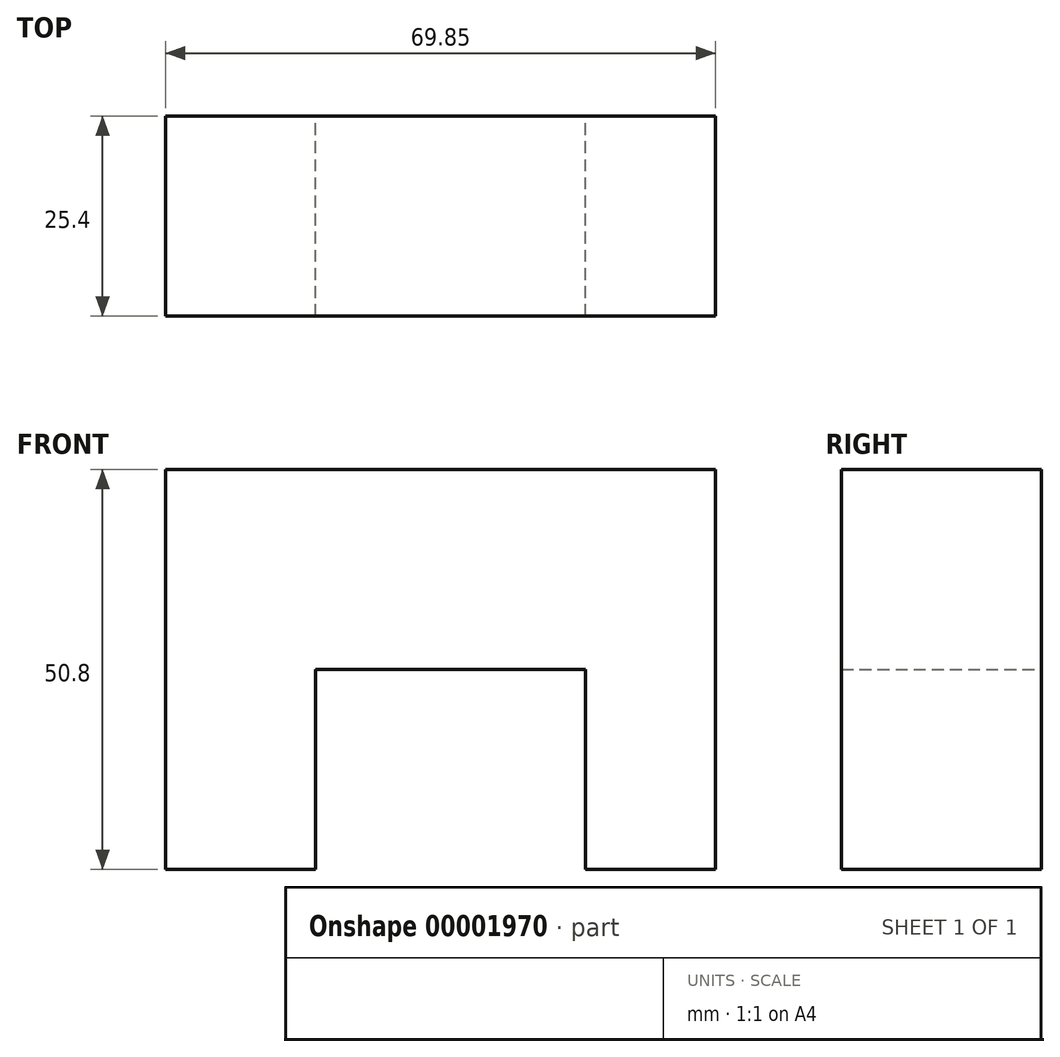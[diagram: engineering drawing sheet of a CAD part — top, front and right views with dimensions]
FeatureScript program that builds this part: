
annotation { "Feature Type Name" : "Feature", "Feature Type Description" : "" }
export const myFeature = defineFeature(function(context is Context, id is Id, definition is map)
    precondition{}
    {
        {
            var Q0;
            Q0=qCreatedBy(makeId("Front.planeOp"),FACE);
            var sketch = newSketch(context, id + "F0", { "sketchPlane" : qUnion([Q0])});
            skLineSegment(sketch, "E0.bottom", {"start": v(0, 0) * mm, "end": v(19.05, 0) * mm});
            skLineSegment(sketch, "E0.top", {"start": v(0, 50.8) * mm, "end": v(69.85, 50.8) * mm});
            skLineSegment(sketch, "E0.left", {"start": v(0, 0) * mm, "end": v(0, 50.8) * mm});
            skLineSegment(sketch, "E0.right", {"start": v(69.85, 0) * mm, "end": v(69.85, 50.8) * mm});
            skLineSegment(sketch, "E1", {"start": v(53.34, 0) * mm, "end": v(53.34, 25.4) * mm});
            skLineSegment(sketch, "E2", {"start": v(53.34, 25.4) * mm, "end": v(19.05, 25.4) * mm});
            skLineSegment(sketch, "E3", {"start": v(19.05, 25.4) * mm, "end": v(19.05, 0) * mm});
            skLineSegment(sketch, "E4.trimOffspring", {"start": v(53.34, 0) * mm, "end": v(69.85, 0) * mm});
            skSolve(sketch);
        }
        {
            var Q0;
            Q0=makeQuery(id+"F0.imprint","IMPRINT",FACE,{"disambiguationData":[TD([[makeQuery(id+"F0.imprint","IMPRINT",EDGE,{"derivedFrom":sQuery(id+"F0.wireOp",EDGE,"E0.bottom")}),1.0]])]});
            extrude(context, id + "F1", {"entities" : qUnion([Q0]), "depth" : 25.4 * mm});
        }
    });
